# Revit family: Hand-Dryer_Bobrick_B-7120
name_source: partatom
category: Electrical Fixtures
revit_build: Autodesk Revit 2015 (Build: 20140223_1515(x64)
units: mm (PartAtom-declared; Revit-internal decimal feet)

## types (1)
- Hand-Dryer_Bobrick_B-7120
    Assembly Code = E1090900
    Cover = Paint-Bobrick-White
    Default Elevation = 4' - 0"
    Description = Bobrick Washroom Accessory as Specified
    Expected Lifespan (Years) = 0
    Installation-Fabrication = http://www.bobrick.com
    Keynote = 102813
    Maintenance Schedule (Months) = 0
    Manufacturer = Bobrick Washroom Equipment, Inc.
    Manufacturer Fax = 818-503-1930
    Manufacturer Website = http://www.bobrick.com
    Model = As Specified
    Product Data = http://arcat.com
    Revision = R1_10_2012
    Sales Information = http://www.bobrick.com
    Send Message = http://www.arcat.com
    Trim = Enamel - Bobrick - Black
    URL = http://www.bobrick.com
    Unit Depth = 0' - 4"
    Unit Height = 1' - 1 19/32"
    Unit Width = 1' - 1 25/32"
    Warranty Duration (Years) = 0

## geometry (parser evidence)
native form markers: Blend x12, Sweep x2
no freeform markers — native parametric forms only
